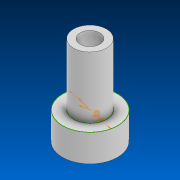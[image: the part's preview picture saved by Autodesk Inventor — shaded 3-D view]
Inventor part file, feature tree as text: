
AUTODESK INVENTOR PART (.ipt)
format: ipt  version: 2022 (Build 260153000, 153)  size: 95,232 bytes
history: native  units: in
note: dims shown in document units (in); Inventor stores cm internally (conversion verified against a paired STEP export)
features: extrude x2, sketch x1
ambient origin geometry x8: Origin, YZ Plane, XZ Plane, XY Plane, X Axis, Y Axis, Z Axis, Center Point
bodies: Solid1 (feature_tree)
feature tree (3):
  sketch  "Sketch1"  dims[d0=0.3in d1=0.18in d2=0.5in d3=0.25in d4=0.0in d5=0.56in d6=0.0in]
  extrude  "Extrusion1"  Depth=0.56in
  extrude  "Extrusion2"  Depth=0.56in
